# Revit family: 248502xx0--Sanitary_Bath-Spas_Roca_MAUI-SQUARE-StonexR-rectangular-bathtub
name_source: partatom
category: Generic Models
units: mm (PartAtom-declared; Revit-internal decimal feet)

## family parameters
Always vertical = No
Can host rebar = No
Cut with Voids When Loaded = No
Part Type = Normal
Room Calculation Point = No
Round Connector Dimension = Use Diameter
Shared = No
Work Plane-Based = No

## types (1)
- MAUI SQUARE - Stonex® rectangular bathtub with click-clack drain and trap
    BIMobject category = Bath & Spas
    BIMobject category code = sanitary-bath-spas
    BIMobject main category = Sanitary
    BIMobject main category code = sanitary
    Brand url = http://www.roca.com
    Design country = Spain
    Edition number = 1
    IFC Classification = Sanitary Terminal
    Manufacturer country = Spain
    Manufacturer name = Roca
    Masterformat 2014 Code = 22 41 19
    Masterformat 2014 Description = Residential Bathtubs
    Material main = Stonex
    NBS Reference Code = 35-06-08
    NBS Reference Description = Baths
    Nominal height = 0 mm  [stored 0 ft]
    Nominal width = 700 mm
    OmniClass Code = 23-31 15 00
    OmniClass Description = Bathtubs
    Product Guid = 74048f52-22ce-477c-bad5-33c2ed31198f
    Product SKU = 248502xx0
    Product data url = https://bimobject.com
    Product family = Maui
    Product group = Bath
    Product url = http://www.roca.com
    QR code = https://www.roca.com
    Technical description = http://www.roca.com
    UNSPSC Code = 30181501
    Uniclass 2015 Code = Pr_40_20_06_08
    Uniclass 2015 Name = Baths
    Uniformat II Code = D2010
    Uniformat II Description = Plumbing Fixtures
    Weight Net (Kg) = 0
    Youtube clip = https://www.youtube.com

note: [stored X ft] marks values corroborated as IEEE doubles in the binary element streams (Revit-internal decimal feet)

## geometry (parser evidence)
native form markers: Blend x4, Sweep x1
no freeform markers — native parametric forms only
